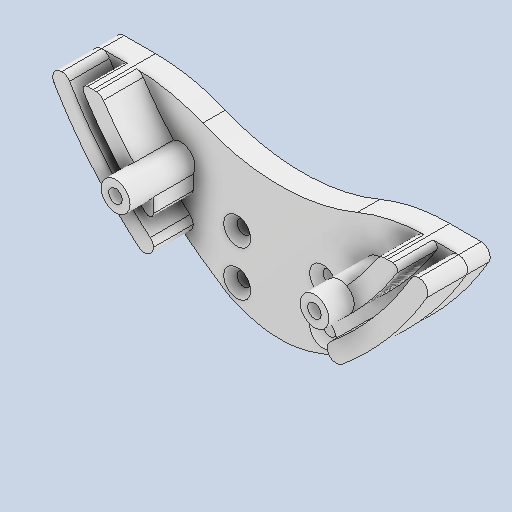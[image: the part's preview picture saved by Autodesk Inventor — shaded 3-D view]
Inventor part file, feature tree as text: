
AUTODESK INVENTOR PART (.ipt)
format: ipt  version: 2023.2 (Build 272271000, 271)  size: 550,400 bytes
history: native  units: mm
features: extrude x4, fillet x4, sketch x3, chamfer x2
ambient origin geometry x8: Origin, YZ Plane, XZ Plane, XY Plane, X Axis, Y Axis, Z Axis, Center Point
bodies: Body1 (feature_tree)
feature tree (13):
  sketch  "Esboço9"  dims[d44=106.0mm d73=4.1mm]
  extrude  "Extrusão4"  Depth=4.1mm
  extrude  "Extrusão5"  Depth=0.1mm
  chamfer  "Chanfro1"  Distance=4.1mm
  extrude  "Extrusão6"  Depth=40.0mm
  fillet  "Arredondamento2"  Radius=0.1mm
  fillet  "Arredondamento3"  Radius=0.1mm
  fillet  "Arredondamento4"  [1 undecoded]
  extrude  "Extrusão7"  Depth=40.0mm
  chamfer  "Chanfro2"  Distance=3.0mm
  fillet  "Arredondamento5"  Radius=6.4mm
  sketch  "Esboço15"  dims[d74=4.1mm d75=0.1mm]
  sketch  "Esboço16"  dims[d76=0.1mm d77=4.1mm d78=4.1mm d79=0.1mm d80=0.1mm d82=90.0deg d83=3.0mm d84=3.0mm d85=6.4mm d93=8.8mm d94=0.0mm d98=4.1mm d99=4.1mm d100=4.1mm d101=4.1mm d102=4.1mm d103=4.1mm d104=4.1mm d105=4.1mm d106=5.0mm d107=0.0mm d108=2.0mm d109=2.0mm d110=45.0deg d111=6.4mm d112=6.4mm d113=5.6mm d114=0.0mm d115=1.0mm d116=2.0mm d117=1.0mm d118=13.5mm d119=0.0mm d120=13.5mm d121=180.0deg d122=20.0mm d123=3.0mm d124=3.0mm d125=3.0mm d126=3.0mm d127=10.0mm d128=4.0mm d129=4.0mm d130=10.0mm d131=0.0mm d132=0.0mm d133=1.5mm d134=2.0mm d135=45.0deg d141=40.0mm d5=0.5mm d6=0.872665mm d7=0.5mm d8=0.872665mm d36=0.5mm d37=0.872665mm d38=0.5mm d39=0.872665mm d86=0.872665mm]
note: 1 required parameter value undecoded (feature->parameter linkage not recoverable at this tier; creation-order binding heuristic only, values carry confidence <= 0.55)
